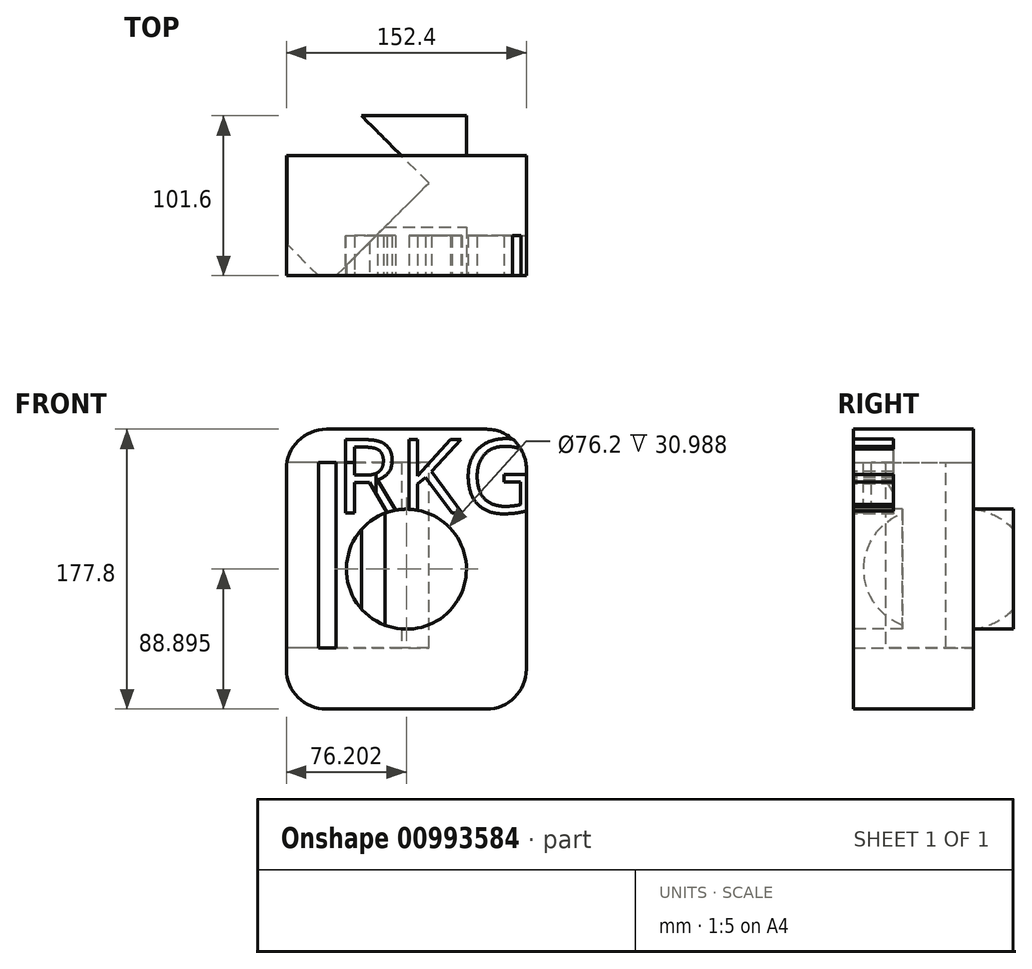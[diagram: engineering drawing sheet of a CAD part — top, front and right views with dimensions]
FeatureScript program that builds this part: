
annotation { "Feature Type Name" : "Feature", "Feature Type Description" : "" }
export const myFeature = defineFeature(function(context is Context, id is Id, definition is map)
    precondition{}
    {
        {
            var Q0;
            Q0=qCreatedBy(makeId("Front.planeOp"),FACE);
            var sketch = newSketch(context, id + "F0", { "sketchPlane" : qUnion([Q0])});
            skLineSegment(sketch, "E0.bottom", {"start": v(-91.39, 121.26) * mm, "end": v(10.21, 121.26) * mm});
            skLineSegment(sketch, "E0.top", {"start": v(-91.39, -56.54) * mm, "end": v(10.21, -56.54) * mm});
            skLineSegment(sketch, "E0.left", {"start": v(-116.79, 95.86) * mm, "end": v(-116.79, -31.14) * mm});
            skLineSegment(sketch, "E0.right", {"start": v(35.61, 95.86) * mm, "end": v(35.61, -31.14) * mm});
            skPoint(sketch, "E1.visualSharp", {"position": v(-116.79, 121.26) * mm});
            skArc(sketch, "E1.filletArc", {"start": v(-91.39, 121.26) * mm, "mid": v(-109.35, 113.82) * mm, "end": v(-116.79, 95.86) * mm});
            skPoint(sketch, "E2.visualSharp", {"position": v(35.61, -56.54) * mm});
            skArc(sketch, "E2.filletArc", {"start": v(10.21, -56.54) * mm, "mid": v(28.17, -49.1) * mm, "end": v(35.61, -31.14) * mm});
            skPoint(sketch, "E3.visualSharp", {"position": v(-116.79, -56.54) * mm});
            skArc(sketch, "E3.filletArc", {"start": v(-116.79, -31.14) * mm, "mid": v(-109.35, -49.1) * mm, "end": v(-91.39, -56.54) * mm});
            skPoint(sketch, "E4.visualSharp", {"position": v(35.61, 121.26) * mm});
            skArc(sketch, "E4.filletArc", {"start": v(35.61, 95.86) * mm, "mid": v(28.17, 113.82) * mm, "end": v(10.21, 121.26) * mm});
            skSolve(sketch);
        }
        {
            var Q0;
            Q0=makeQuery(id+"F0.imprint","IMPRINT",FACE,{"disambiguationData":[TD([[makeQuery(id+"F0.imprint","IMPRINT",EDGE,{"derivedFrom":sQuery(id+"F0.wireOp",EDGE,"E0.bottom")}),-1.0]])]});
            extrude(context, id + "F1", {"entities" : qUnion([Q0]), "depth" : 76.2 * mm, "offsetDistance" : 25.4 * mm});
        }
        {
            var Q0;
            Q0=makeQuery(id+"F1.opExtrude","CAP_FACE",FACE,{"disambiguationData":[OSD([sQuery(id+"F0.wireOp",EDGE,"E0.bottom"),sQuery(id+"F0.wireOp",EDGE,"E0.top"),sQuery(id+"F0.wireOp",EDGE,"E0.left"),sQuery(id+"F0.wireOp",EDGE,"E0.right"),sQuery(id+"F0.wireOp",EDGE,"E1.filletArc"),sQuery(id+"F0.wireOp",EDGE,"E2.filletArc"),sQuery(id+"F0.wireOp",EDGE,"E3.filletArc"),sQuery(id+"F0.wireOp",EDGE,"E4.filletArc")])],"isStart":false});
            var sketch = newSketch(context, id + "F2", { "sketchPlane" : qUnion([Q0])});
            skCircle(sketch, "E5", {"center": v(-40.59, 32.36) * mm, "radius": 38.1 * mm});
            skPoint(sketch, "E5.third.point", {"position": v(-34.95, -56.54) * mm});
            skLineSegment(sketch, "E6", {"start": v(-40.59, 121.26) * mm, "end": v(-40.59, -56.54) * mm, "construction": true});
            skLineSegment(sketch, "E7", {"start": v(-116.79, 32.36) * mm, "end": v(35.61, 32.36) * mm, "construction": true});
            skSolve(sketch);
        }
        {
            var Q0;
            Q0=makeQuery(id+"F2.imprint","IMPRINT",FACE,{"disambiguationData":[TD([[makeQuery(id+"F2.imprint","IMPRINT",EDGE,{"derivedFrom":sQuery(id+"F2.wireOp",EDGE,"E5")}),1.0]])]});
            extrude(context, id + "F3", {"entities" : qUnion([Q0]), "operationType" : NewBodyOperationType.REMOVE, "oppositeDirection" : true, "depth" : 30.99 * mm, "offsetDistance" : 25.4 * mm});
        }
        {
            var Q0;
            Q0=makeQuery(id+"F1.opExtrude","CAP_FACE",FACE,{"disambiguationData":[OSD([sQuery(id+"F0.wireOp",EDGE,"E0.bottom"),sQuery(id+"F0.wireOp",EDGE,"E0.top"),sQuery(id+"F0.wireOp",EDGE,"E0.left"),sQuery(id+"F0.wireOp",EDGE,"E0.right"),sQuery(id+"F0.wireOp",EDGE,"E1.filletArc"),sQuery(id+"F0.wireOp",EDGE,"E2.filletArc"),sQuery(id+"F0.wireOp",EDGE,"E3.filletArc"),sQuery(id+"F0.wireOp",EDGE,"E4.filletArc")])],"isStart":true});
            var sketch = newSketch(context, id + "F4", { "sketchPlane" : qUnion([Q0])});
            skCircle(sketch, "E8.0", {"center": v(40.59, 32.36) * mm, "radius": 38.1 * mm});
            skSolve(sketch);
        }
        {
            var Q0;
            Q0=makeQuery(id+"F4.imprint","IMPRINT",FACE,{"disambiguationData":[TD([[makeQuery(id+"F4.imprint","IMPRINT",EDGE,{"derivedFrom":sQuery(id+"F4.wireOp",EDGE,"E8.0")}),1.0]])]});
            extrude(context, id + "F5", {"entities" : qUnion([Q0]), "operationType" : NewBodyOperationType.ADD, "depth" : 25.4 * mm, "offsetDistance" : 25.4 * mm});
        }
        {
            var Q0;
            Q0=makeQuery(id+"F1.opExtrude","CAP_EDGE",EDGE,{"disambiguationData":[OSD([sQuery(id+"F0.wireOp",EDGE,"E0.left")])],"isStart":true});
            cPlane(context, id + "F6", {"entities" : qUnion([Q0]), "cplaneType" : CPlaneType.LINE_ANGLE, "offset" : 25.4 * mm, "angle" : 45 * degree, "width" : 152.4 * mm, "height" : 152.4 * mm});
        }
        {
            var Q0;
            Q0=qCreatedBy(id+"F6.planeOp",FACE);
            var sketch = newSketch(context, id + "F7", { "sketchPlane" : qUnion([Q0])});
            skLineSegment(sketch, "E9.bottom", {"start": v(122.04, -17.64) * mm, "end": v(30.87, -17.64) * mm});
            skLineSegment(sketch, "E9.top", {"start": v(122.04, 100.02) * mm, "end": v(30.87, 100.02) * mm});
            skLineSegment(sketch, "E9.left", {"start": v(122.04, -17.64) * mm, "end": v(122.04, 100.02) * mm});
            skLineSegment(sketch, "E9.right", {"start": v(30.87, -17.64) * mm, "end": v(30.87, 100.02) * mm});
            skSolve(sketch);
        }
        {
            var Q0;
            Q0 = qSketchRegion(id + "F7", true);
            extrude(context, id + "F8", {"entities" : qUnion([Q0]), "operationType" : NewBodyOperationType.REMOVE, "oppositeDirection" : true, "depth" : 76.2 * mm, "offsetDistance" : 25.4 * mm});
        }
        {
            var Q0;
            Q0=makeQuery(id+"F1.opExtrude","CAP_FACE",FACE,{"disambiguationData":[OSD([sQuery(id+"F0.wireOp",EDGE,"E0.bottom"),sQuery(id+"F0.wireOp",EDGE,"E0.top"),sQuery(id+"F0.wireOp",EDGE,"E0.left"),sQuery(id+"F0.wireOp",EDGE,"E0.right"),sQuery(id+"F0.wireOp",EDGE,"E1.filletArc"),sQuery(id+"F0.wireOp",EDGE,"E2.filletArc"),sQuery(id+"F0.wireOp",EDGE,"E3.filletArc"),sQuery(id+"F0.wireOp",EDGE,"E4.filletArc")])],"isStart":false});
            var sketch = newSketch(context, id + "F9", { "sketchPlane" : qUnion([Q0])});
            skText(sketch, "E10", { "text": "RKG\n", "fontName": "OpenSans-Regular.ttf"});
            const initialGuessF9  = {"E10": [-0.08548, 0.06816, 1, 0, 0.04685]};
            skSetInitialGuess(sketch, initialGuessF9);
            skSolve(sketch);
        }
        {
            var Q0;
            Q0 = qSketchRegion(id + "F9", true);
            extrude(context, id + "F10", {"entities" : qUnion([Q0]), "operationType" : NewBodyOperationType.REMOVE, "oppositeDirection" : true, "depth" : 25.4 * mm, "offsetDistance" : 25.4 * mm});
        }
    });
